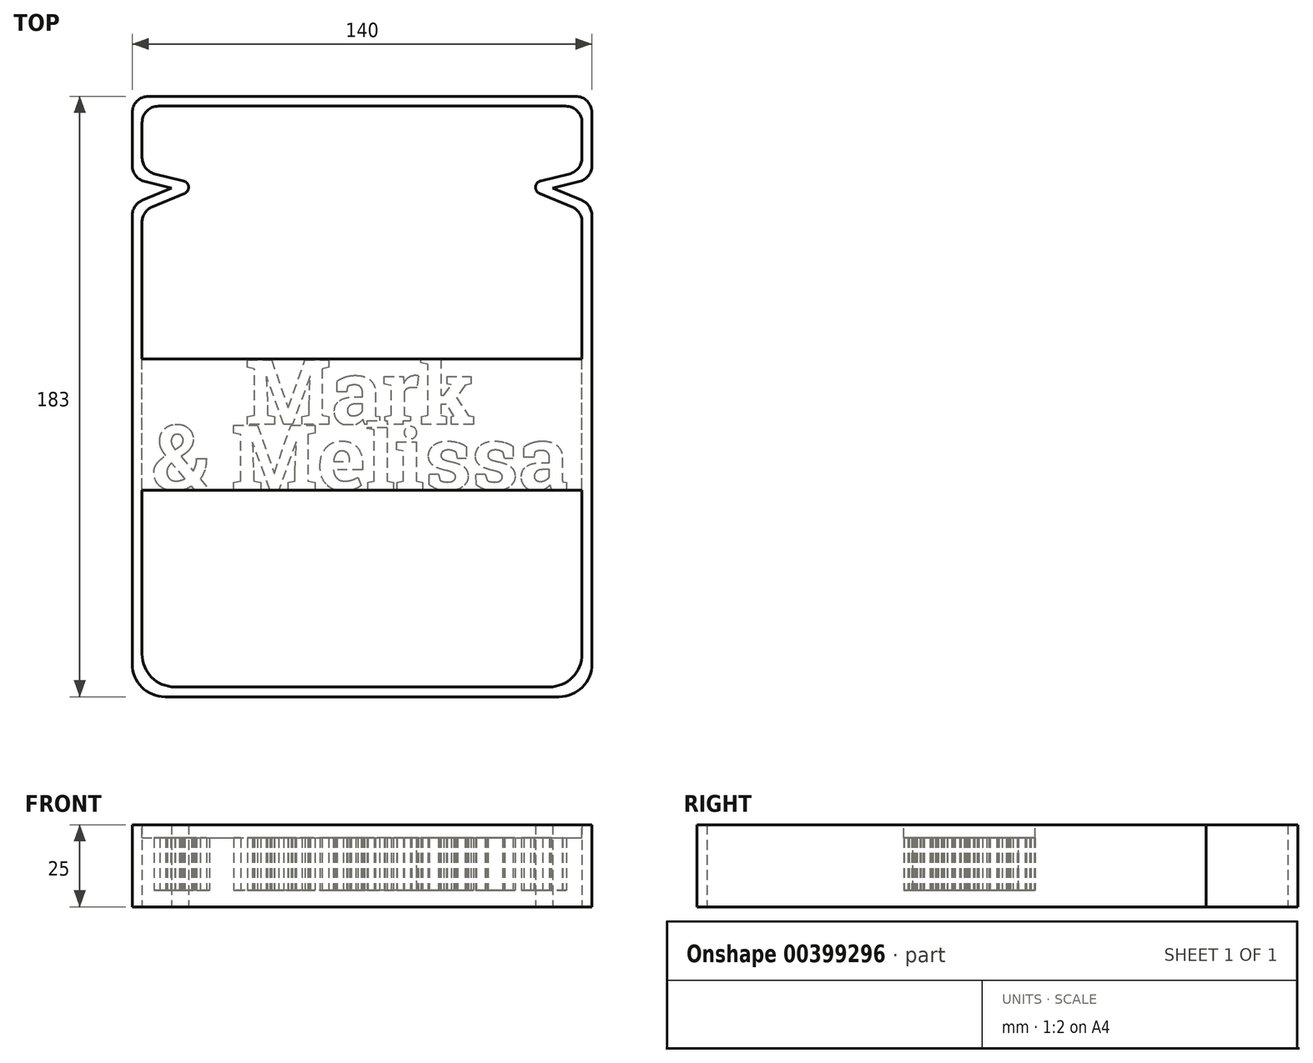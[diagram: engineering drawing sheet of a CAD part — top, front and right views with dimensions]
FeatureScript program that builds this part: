
annotation { "Feature Type Name" : "Feature", "Feature Type Description" : "" }
export const myFeature = defineFeature(function(context is Context, id is Id, definition is map)
    precondition{}
    {
        {
            var Q0;
            Q0=qCreatedBy(makeId("Top.planeOp"),FACE);
            var sketch = newSketch(context, id + "F0", { "sketchPlane" : qUnion([Q0])});
            skText(sketch, "E0", { "text": "Mark", "fontName": "RobotoSlab-Bold.ttf"});
            skText(sketch, "E1", { "text": "& Melissa", "fontName": "RobotoSlab-Bold.ttf"});
            skLineSegment(sketch, "E2.bottom", {"start": v(-64, -20) * mm, "end": v(64, -20) * mm});
            skLineSegment(sketch, "E2.top", {"start": v(-64, 0) * mm, "end": v(64, 0) * mm});
            skLineSegment(sketch, "E2.left", {"start": v(-64, -20) * mm, "end": v(-64, 0) * mm});
            skLineSegment(sketch, "E2.right", {"start": v(64, -20) * mm, "end": v(64, 0) * mm});
            skLineSegment(sketch, "E3.bottom", {"start": v(-35.61, 20) * mm, "end": v(35.61, 20) * mm});
            skLineSegment(sketch, "E3.top", {"start": v(-35.61, 0) * mm, "end": v(35.61, 0) * mm});
            skLineSegment(sketch, "E3.left", {"start": v(-35.61, 20) * mm, "end": v(-35.61, 0) * mm});
            skLineSegment(sketch, "E3.right", {"start": v(35.61, 20) * mm, "end": v(35.61, 0) * mm});
            skLineSegment(sketch, "E4.bottom", {"start": v(17, 0) * mm, "end": v(12.5, 0) * mm});
            skLineSegment(sketch, "E4.top", {"start": v(17, -1) * mm, "end": v(12.5, -1) * mm});
            skLineSegment(sketch, "E4.left", {"start": v(17, 0) * mm, "end": v(17, -1) * mm});
            skLineSegment(sketch, "E4.right", {"start": v(12.5, 0) * mm, "end": v(12.5, -1) * mm});
            skLineSegment(sketch, "E5.bottom", {"start": v(8, 0) * mm, "end": v(1, 0) * mm});
            skLineSegment(sketch, "E5.top", {"start": v(8, -1) * mm, "end": v(1, -1) * mm});
            skLineSegment(sketch, "E5.left", {"start": v(8, 0) * mm, "end": v(8, -1) * mm});
            skLineSegment(sketch, "E5.right", {"start": v(1, 0) * mm, "end": v(1, -1) * mm});
            skCircle(sketch, "E6", {"center": v(14.75, -2.5) * mm, "radius": 1.9 * mm});
            skPoint(sketch, "E6.centerSnap0", {"position": v(14.75, -1) * mm});
            const initialGuessF0  = {"E0": [-0.03561, 0, 1, 0, 0.02], "E1": [-0.064, -0.02, 1, 0, 0.02]};
            skSetInitialGuess(sketch, initialGuessF0);
            skSolve(sketch);
        }
        {
            var Q0;
            {var subQ1=sQuery(id+"F0.wireOp",EDGE,"E1.sketch_text.stroke-181");Q0=makeQuery(id+"F0.imprint","IMPRINT",FACE,{"disambiguationData":[TD([[makeQuery(id+"F0.imprint","IMPRINT",EDGE,{"derivedFrom":subQ1}),-1.0]])]});}
            var Q1;
            Q1=makeQuery(id+"F0.imprint","IMPRINT",FACE,{"disambiguationData":[TD([[makeQuery(id+"F0.imprint","IMPRINT",EDGE,{"derivedFrom":sQuery(id+"F0.wireOp",EDGE,"E1.sketch_text.stroke-151")}),-1.0]])]});
            var Q2;
            Q2=makeQuery(id+"F0.imprint","IMPRINT",FACE,{"disambiguationData":[TD([[makeQuery(id+"F0.imprint","IMPRINT",EDGE,{"derivedFrom":sQuery(id+"F0.wireOp",EDGE,"E1.sketch_text.stroke-121")}),-1.0]])]});
            var Q3;
            Q3=makeQuery(id+"F0.imprint","IMPRINT",FACE,{"disambiguationData":[TD([[makeQuery(id+"F0.imprint","IMPRINT",EDGE,{"derivedFrom":sQuery(id+"F0.wireOp",EDGE,"E1.sketch_text.stroke-107")}),-1.0]])]});
            var Q4;
            {var subQ8=sQuery(id+"F0.wireOp",EDGE,"E1.sketch_text.stroke-100");Q4=makeQuery(id+"F0.imprint","IMPRINT",FACE,{"disambiguationData":[TD([[makeQuery(id+"F0.imprint","IMPRINT",EDGE,{"derivedFrom":subQ8}),-1.0]])]});}
            var Q5;
            {var subQ4=sQuery(id+"F0.wireOp",EDGE,"E1.sketch_text.stroke-74");Q5=makeQuery(id+"F0.imprint","IMPRINT",FACE,{"disambiguationData":[TD([[makeQuery(id+"F0.imprint","IMPRINT",EDGE,{"derivedFrom":subQ4}),-1.0]])]});}
            var Q6;
            Q6=makeQuery(id+"F0.imprint","IMPRINT",FACE,{"disambiguationData":[TD([[makeQuery(id+"F0.imprint","IMPRINT",EDGE,{"derivedFrom":sQuery(id+"F0.wireOp",EDGE,"E1.sketch_text.stroke-42")}),-1.0]])]});
            var Q7;
            Q7=makeQuery(id+"F0.imprint","IMPRINT",FACE,{"disambiguationData":[TD([[makeQuery(id+"F0.imprint","IMPRINT",EDGE,{"derivedFrom":sQuery(id+"F0.wireOp",EDGE,"E1.sketch_text.stroke-0")}),-1.0]])]});
            var Q8;
            Q8=makeQuery(id+"F0.imprint","IMPRINT",FACE,{"disambiguationData":[TD([[makeQuery(id+"F0.imprint","IMPRINT",EDGE,{"derivedFrom":sQuery(id+"F0.wireOp",EDGE,"E0.sketch_text.stroke-0")}),-1.0]])]});
            var Q9;
            {var subQ4=sQuery(id+"F0.wireOp",EDGE,"E0.sketch_text.stroke-31");Q9=makeQuery(id+"F0.imprint","IMPRINT",FACE,{"disambiguationData":[TD([[makeQuery(id+"F0.imprint","IMPRINT",EDGE,{"derivedFrom":subQ4}),-1.0]])]});}
            var Q10;
            {var subQ1=sQuery(id+"F0.wireOp",EDGE,"E0.sketch_text.stroke-66");Q10=makeQuery(id+"F0.imprint","IMPRINT",FACE,{"disambiguationData":[TD([[makeQuery(id+"F0.imprint","IMPRINT",EDGE,{"derivedFrom":subQ1}),-1.0]])]});}
            var Q11;
            {var subQ5=sQuery(id+"F0.wireOp",EDGE,"E0.sketch_text.stroke-88");Q11=makeQuery(id+"F0.imprint","IMPRINT",FACE,{"disambiguationData":[TD([[makeQuery(id+"F0.imprint","IMPRINT",EDGE,{"derivedFrom":subQ5}),-1.0]])]});}
            var Q12;
            {var subQ0=sQuery(id+"F0.wireOp",EDGE,"E6");var subQ1=sQuery(id+"F0.wireOp",EDGE,"E1.sketch_text.stroke-117");var subQ2=makeQuery(id+"F0.imprint","INTERSECT",VERTEX,{"disambiguationData":[OD(0.0)],"derivedFrom":[subQ1,subQ0]});Q12=makeQuery(id+"F0.imprint","IMPRINT",FACE,{"disambiguationData":[TD([[makeQuery(id+"F0.imprint","IMPRINT",EDGE,{"disambiguationData":[TD([[subQ2,-1.0]])],"derivedFrom":subQ1}),1.0]])]});}
            var Q13;
            {var subQ0=sQuery(id+"F0.wireOp",EDGE,"E6");var subQ1=sQuery(id+"F0.wireOp",EDGE,"E1.sketch_text.stroke-117");var subQ2=makeQuery(id+"F0.imprint","INTERSECT",VERTEX,{"disambiguationData":[OD(0.0)],"derivedFrom":[subQ1,subQ0]});Q13=makeQuery(id+"F0.imprint","IMPRINT",FACE,{"disambiguationData":[TD([[makeQuery(id+"F0.imprint","IMPRINT",EDGE,{"disambiguationData":[TD([[subQ2,-1.0]])],"derivedFrom":subQ1}),-1.0]])]});}
            var Q14;
            {var subQ0=sQuery(id+"F0.wireOp",EDGE,"E6");var subQ1=sQuery(id+"F0.wireOp",EDGE,"E4.top");var subQ2=makeQuery(id+"F0.imprint","INTERSECT",VERTEX,{"disambiguationData":[OD(0.0)],"derivedFrom":[subQ1,subQ0]});Q14=makeQuery(id+"F0.imprint","IMPRINT",FACE,{"disambiguationData":[TD([[makeQuery(id+"F0.imprint","IMPRINT",EDGE,{"disambiguationData":[TD([[subQ2,-1.0]])],"derivedFrom":subQ1}),-1.0]])]});}
            extrude(context, id + "F1", {"entities" : qUnion([Q0, Q1, Q2, Q3, Q4, Q5, Q6, Q7, Q8, Q9, Q10, Q11, Q12, Q13, Q14]), "depth" : 24 * mm, "hasSecondDirection" : true, "secondDirectionOppositeDirection" : false, "secondDirectionDepth" : 5 * mm});
        }
        {
            var Q0;
            Q0=qCreatedBy(makeId("Top.planeOp"),FACE);
            var sketch = newSketch(context, id + "F2", { "sketchPlane" : qUnion([Q0])});
            skLineSegment(sketch, "E7.bottom", {"start": v(-70, -83) * mm, "end": v(70, -83) * mm});
            skLineSegment(sketch, "E7.top", {"start": v(-70, 100) * mm, "end": v(70, 100) * mm});
            skLineSegment(sketch, "E7.right", {"start": v(70, -83) * mm, "end": v(70, 67) * mm});
            skLineSegment(sketch, "E8", {"start": v(-70, 75) * mm, "end": v(-58, 72) * mm});
            skLineSegment(sketch, "E9", {"start": v(-58, 72) * mm, "end": v(-70, 67) * mm});
            skLineSegment(sketch, "E10.MirrorCS", {"start": v(58, 72) * mm, "end": v(70, 67) * mm});
            skLineSegment(sketch, "E11.MirrorCS", {"start": v(70, 75) * mm, "end": v(58, 72) * mm});
            skLineSegment(sketch, "E12.trimOffspring", {"start": v(-70, 75) * mm, "end": v(-70, 100) * mm});
            skLineSegment(sketch, "E13.trimOffspring", {"start": v(70, 75) * mm, "end": v(70, 100) * mm});
            skLineSegment(sketch, "E14", {"start": v(-70, 67) * mm, "end": v(-70, -83) * mm});
            skLineSegment(sketch, "E15.bottom", {"start": v(-67, -80) * mm, "end": v(0, -80) * mm});
            skLineSegment(sketch, "E15.left", {"start": v(-67, -80) * mm, "end": v(-67, 65) * mm});
            skLineSegment(sketch, "E16.bottom", {"start": v(-67, 97) * mm, "end": v(0, 97) * mm});
            skLineSegment(sketch, "E16.left", {"start": v(-67, 97) * mm, "end": v(-67, 77.34) * mm});
            skLineSegment(sketch, "E17", {"start": v(-48.49, 72.71) * mm, "end": v(-67, 77.34) * mm});
            skLineSegment(sketch, "E18", {"start": v(0, 97) * mm, "end": v(0, -80) * mm, "construction": true});
            skLineSegment(sketch, "E19", {"start": v(-67, 65) * mm, "end": v(-48.49, 72.71) * mm});
            skLineSegment(sketch, "E20.MirrorCS", {"start": v(67, 97) * mm, "end": v(0, 97) * mm});
            skLineSegment(sketch, "E21.MirrorCS", {"start": v(67, 97) * mm, "end": v(67, 77.34) * mm});
            skLineSegment(sketch, "E22.MirrorCS", {"start": v(48.49, 72.71) * mm, "end": v(67, 77.34) * mm});
            skLineSegment(sketch, "E23.MirrorCS", {"start": v(67, 65) * mm, "end": v(48.49, 72.71) * mm});
            skLineSegment(sketch, "E24.MirrorCS", {"start": v(67, -80) * mm, "end": v(67, 65) * mm});
            skLineSegment(sketch, "E25.MirrorCS", {"start": v(67, -80) * mm, "end": v(0, -80) * mm});
            skSolve(sketch);
        }
        {
            var Q0;
            Q0=makeQuery(id+"F2.imprint","IMPRINT",FACE,{"disambiguationData":[TD([[makeQuery(id+"F2.imprint","IMPRINT",EDGE,{"derivedFrom":sQuery(id+"F2.wireOp",EDGE,"E7.bottom")}),1.0]])]});
            extrude(context, id + "F3", {"entities" : qUnion([Q0]), "operationType" : NewBodyOperationType.ADD, "depth" : 25 * mm});
        }
        {
            var Q0;
            Q0=makeQuery(id+"F3.opExtrude","CAP_FACE",FACE,{"disambiguationData":[OSD([sQuery(id+"F2.wireOp",EDGE,"E7.bottom"),sQuery(id+"F2.wireOp",EDGE,"E7.top"),sQuery(id+"F2.wireOp",EDGE,"E7.right"),sQuery(id+"F2.wireOp",EDGE,"E8"),sQuery(id+"F2.wireOp",EDGE,"E9"),sQuery(id+"F2.wireOp",EDGE,"E10.MirrorCS"),sQuery(id+"F2.wireOp",EDGE,"E11.MirrorCS"),sQuery(id+"F2.wireOp",EDGE,"E12.trimOffspring"),sQuery(id+"F2.wireOp",EDGE,"E13.trimOffspring"),sQuery(id+"F2.wireOp",EDGE,"E14"),sQuery(id+"F2.wireOp",EDGE,"E15.bottom"),sQuery(id+"F2.wireOp",EDGE,"E15.left"),sQuery(id+"F2.wireOp",EDGE,"E16.bottom"),sQuery(id+"F2.wireOp",EDGE,"E16.left"),sQuery(id+"F2.wireOp",EDGE,"E17"),sQuery(id+"F2.wireOp",EDGE,"E19"),sQuery(id+"F2.wireOp",EDGE,"E20.MirrorCS"),sQuery(id+"F2.wireOp",EDGE,"E21.MirrorCS"),sQuery(id+"F2.wireOp",EDGE,"E22.MirrorCS"),sQuery(id+"F2.wireOp",EDGE,"E23.MirrorCS"),sQuery(id+"F2.wireOp",EDGE,"E24.MirrorCS"),sQuery(id+"F2.wireOp",EDGE,"E25.MirrorCS")])],"isStart":false});
            var sketch = newSketch(context, id + "F4", { "sketchPlane" : qUnion([Q0])});
            skLineSegment(sketch, "E26.bottom", {"start": v(-70, 20) * mm, "end": v(70, 20) * mm});
            skLineSegment(sketch, "E26.top", {"start": v(-70, -20) * mm, "end": v(70, -20) * mm});
            skLineSegment(sketch, "E26.left", {"start": v(-70, 20) * mm, "end": v(-70, -20) * mm});
            skLineSegment(sketch, "E26.right", {"start": v(70, 20) * mm, "end": v(70, -20) * mm});
            skSolve(sketch);
        }
        {
            var Q0;
            {var subQ0=sQuery(id+"F4.wireOp",EDGE,"E26.bottom");var subQ1=makeQuery(id+"F3.opExtrude","CAP_EDGE",EDGE,{"disambiguationData":[OSD([sQuery(id+"F2.wireOp",EDGE,"E15.left")])],"isStart":false});var subQ2=makeQuery(id+"F4.imprint","INTERSECT",VERTEX,{"derivedFrom":[subQ1,subQ0]});Q0=makeQuery(id+"F4.imprint","IMPRINT",FACE,{"disambiguationData":[TD([[makeQuery(id+"F4.imprint","IMPRINT",EDGE,{"disambiguationData":[TD([[subQ2,-1.0]])],"derivedFrom":subQ0}),-1.0]])]});}
            extrude(context, id + "F5", {"entities" : qUnion([Q0]), "operationType" : NewBodyOperationType.ADD, "oppositeDirection" : true, "depth" : 4 * mm});
        }
        {
            var Q0;
            Q0=makeQuery(id+"F3.opExtrude","SWEPT_EDGE",EDGE,{"disambiguationData":[OSD([sQuery(id+"F2.wireOp",EDGE,"E15.bottom"),sQuery(id+"F2.wireOp",EDGE,"E15.left")])]});
            var Q1;
            Q1=makeQuery(id+"F3.opExtrude","SWEPT_EDGE",EDGE,{"disambiguationData":[OSD([sQuery(id+"F2.wireOp",EDGE,"E24.MirrorCS"),sQuery(id+"F2.wireOp",EDGE,"E25.MirrorCS")])]});
            var Q2;
            Q2=makeQuery(id+"F3.opExtrude","SWEPT_EDGE",EDGE,{"disambiguationData":[OSD([sQuery(id+"F2.wireOp",EDGE,"E7.bottom"),sQuery(id+"F2.wireOp",EDGE,"E7.right")])]});
            var Q3;
            Q3=makeQuery(id+"F3.opExtrude","SWEPT_EDGE",EDGE,{"disambiguationData":[OSD([sQuery(id+"F2.wireOp",EDGE,"E7.bottom"),sQuery(id+"F2.wireOp",EDGE,"E14")])]});
            fillet(context, id + "F6", {"entities" : qUnion([Q0, Q1, Q2, Q3]), "radius" : 10 * mm, "tangentPropagation" : true, "allowEdgeOverflow" : false});
        }
        {
            var Q0;
            Q0=makeQuery(id+"F3.opExtrude","SWEPT_EDGE",EDGE,{"disambiguationData":[OSD([sQuery(id+"F2.wireOp",EDGE,"E7.top"),sQuery(id+"F2.wireOp",EDGE,"E12.trimOffspring")])]});
            var Q1;
            Q1=makeQuery(id+"F3.opExtrude","SWEPT_EDGE",EDGE,{"disambiguationData":[OSD([sQuery(id+"F2.wireOp",EDGE,"E16.bottom"),sQuery(id+"F2.wireOp",EDGE,"E16.left")])]});
            var Q2;
            Q2=makeQuery(id+"F3.opExtrude","SWEPT_EDGE",EDGE,{"disambiguationData":[OSD([sQuery(id+"F2.wireOp",EDGE,"E7.top"),sQuery(id+"F2.wireOp",EDGE,"E13.trimOffspring")])]});
            var Q3;
            Q3=makeQuery(id+"F3.opExtrude","SWEPT_EDGE",EDGE,{"disambiguationData":[OSD([sQuery(id+"F2.wireOp",EDGE,"E20.MirrorCS"),sQuery(id+"F2.wireOp",EDGE,"E21.MirrorCS")])]});
            var Q4;
            Q4=makeQuery(id+"F3.opExtrude","SWEPT_EDGE",EDGE,{"disambiguationData":[OSD([sQuery(id+"F2.wireOp",EDGE,"E21.MirrorCS"),sQuery(id+"F2.wireOp",EDGE,"E22.MirrorCS")])]});
            var Q5;
            Q5=makeQuery(id+"F3.opExtrude","SWEPT_EDGE",EDGE,{"disambiguationData":[OSD([sQuery(id+"F2.wireOp",EDGE,"E11.MirrorCS"),sQuery(id+"F2.wireOp",EDGE,"E13.trimOffspring")])]});
            var Q6;
            Q6=makeQuery(id+"F3.opExtrude","SWEPT_EDGE",EDGE,{"disambiguationData":[OSD([sQuery(id+"F2.wireOp",EDGE,"E16.left"),sQuery(id+"F2.wireOp",EDGE,"E17")])]});
            var Q7;
            Q7=makeQuery(id+"F3.opExtrude","SWEPT_EDGE",EDGE,{"disambiguationData":[OSD([sQuery(id+"F2.wireOp",EDGE,"E8"),sQuery(id+"F2.wireOp",EDGE,"E12.trimOffspring")])]});
            var Q8;
            Q8=makeQuery(id+"F3.opExtrude","SWEPT_EDGE",EDGE,{"disambiguationData":[OSD([sQuery(id+"F2.wireOp",EDGE,"E7.right"),sQuery(id+"F2.wireOp",EDGE,"E10.MirrorCS")])]});
            var Q9;
            Q9=makeQuery(id+"F3.opExtrude","SWEPT_EDGE",EDGE,{"disambiguationData":[OSD([sQuery(id+"F2.wireOp",EDGE,"E23.MirrorCS"),sQuery(id+"F2.wireOp",EDGE,"E24.MirrorCS")])]});
            var Q10;
            Q10=makeQuery(id+"F3.opExtrude","SWEPT_EDGE",EDGE,{"disambiguationData":[OSD([sQuery(id+"F2.wireOp",EDGE,"E9"),sQuery(id+"F2.wireOp",EDGE,"E14")])]});
            var Q11;
            Q11=makeQuery(id+"F3.opExtrude","SWEPT_EDGE",EDGE,{"disambiguationData":[OSD([sQuery(id+"F2.wireOp",EDGE,"E15.left"),sQuery(id+"F2.wireOp",EDGE,"E19")])]});
            fillet(context, id + "F7", {"entities" : qUnion([Q0, Q1, Q2, Q3, Q4, Q5, Q6, Q7, Q8, Q9, Q10, Q11]), "radius" : 5 * mm, "tangentPropagation" : true, "allowEdgeOverflow" : false});
        }
        {
            var Q0;
            Q0=makeQuery(id+"F3.opExtrude","SWEPT_EDGE",EDGE,{"disambiguationData":[OSD([sQuery(id+"F2.wireOp",EDGE,"E22.MirrorCS"),sQuery(id+"F2.wireOp",EDGE,"E23.MirrorCS")])]});
            var Q1;
            Q1=makeQuery(id+"F3.opExtrude","SWEPT_EDGE",EDGE,{"disambiguationData":[OSD([sQuery(id+"F2.wireOp",EDGE,"E17"),sQuery(id+"F2.wireOp",EDGE,"E19")])]});
            fillet(context, id + "F8", {"entities" : qUnion([Q0, Q1]), "radius" : 2 * mm, "tangentPropagation" : true, "allowEdgeOverflow" : false});
        }
    });
